# Revit family: BVN_BKKF
name_source: partatom
category: Mechanical Equipment
units: mm (PartAtom-declared; Revit-internal decimal feet)

## family parameters
Always vertical = Yes
Cut with Voids When Loaded = No
OmniClass Number = 23.75.00.00
OmniClass Title = Climate Control (HVAC)
Part Type = Breaks Into
Room Calculation Point = No
Round Connector Dimension = Use Diameter
Shared = No
Work Plane-Based = No

## types (4) — shared parameters
Description = Duct Fan
Frequency = 50 Hz
Insulation Class = F
Manufacturer = Bahçıvan Elektrik Motor San. ve Tic. Ltd. Şti.
Material = <By Category>
Model = BKKF
Protection Class = 44
URL = http://www.bahcivanmotor.com.tr

## per-type parameters (varying)
| type | A | Air Flow | B | C | Capacitor (uF) | Current | D | D' | D'' | Dh | Dh' | Power | Sound Pressure Level dB(A) | Speed ( d/d ) | Voltage | Weight |
| BKKF 400 | 670 mm  [stored 2.19816 ft] | 4800.0 m³/h | 670 mm  [stored 2.19816 ft] | 610 mm | 10 | 2 A | 382 mm  [stored 1.25328 ft] | 287 mm | 191 mm  [stored 0.62664 ft] | 168 mm | 84 mm | 460 W | 45 | 1600 | 230 V | 36.00 kg |
| BKKF 450 | 670 mm  [stored 2.19816 ft] | 6000.0 m³/h | 670 mm  [stored 2.19816 ft] | 610 mm | 10 | 4 A | 283 mm  [stored 0.928478 ft] | 212 mm | 142 mm | 168 mm | 84 mm | 745 W | 48 | 1550 | 230 V | 40.00 kg |
| BKKF 500 | 670 mm  [stored 2.19816 ft] | 7800.0 m³/h | 670 mm  [stored 2.19816 ft] | 610 mm | 0 | 2 A | 344 mm  [stored 1.12861 ft] | 258 mm | 172 mm  [stored 0.564304 ft] | 168 mm | 84 mm | 960 W | 52 | 1335 | 380 V | 51.00 kg |
| BKKF 560 | 800 mm  [stored 2.62467 ft] | 9800.0 m³/h | 800 mm  [stored 2.62467 ft] | 740 mm  [stored 2.42782 ft] | 0 | 3 A | 382 mm  [stored 1.25328 ft] | 287 mm | 191 mm  [stored 0.62664 ft] | 200 mm  [stored 0.656168 ft] | 100 mm  [stored 0.328084 ft] | 1400 W | 55 | 1250 | 380 V | 65.00 kg |

note: [stored X ft] marks values corroborated as IEEE doubles in the binary element streams (Revit-internal decimal feet)

## geometry (parser evidence)
native form markers: Sweep x3
no freeform markers — native parametric forms only
